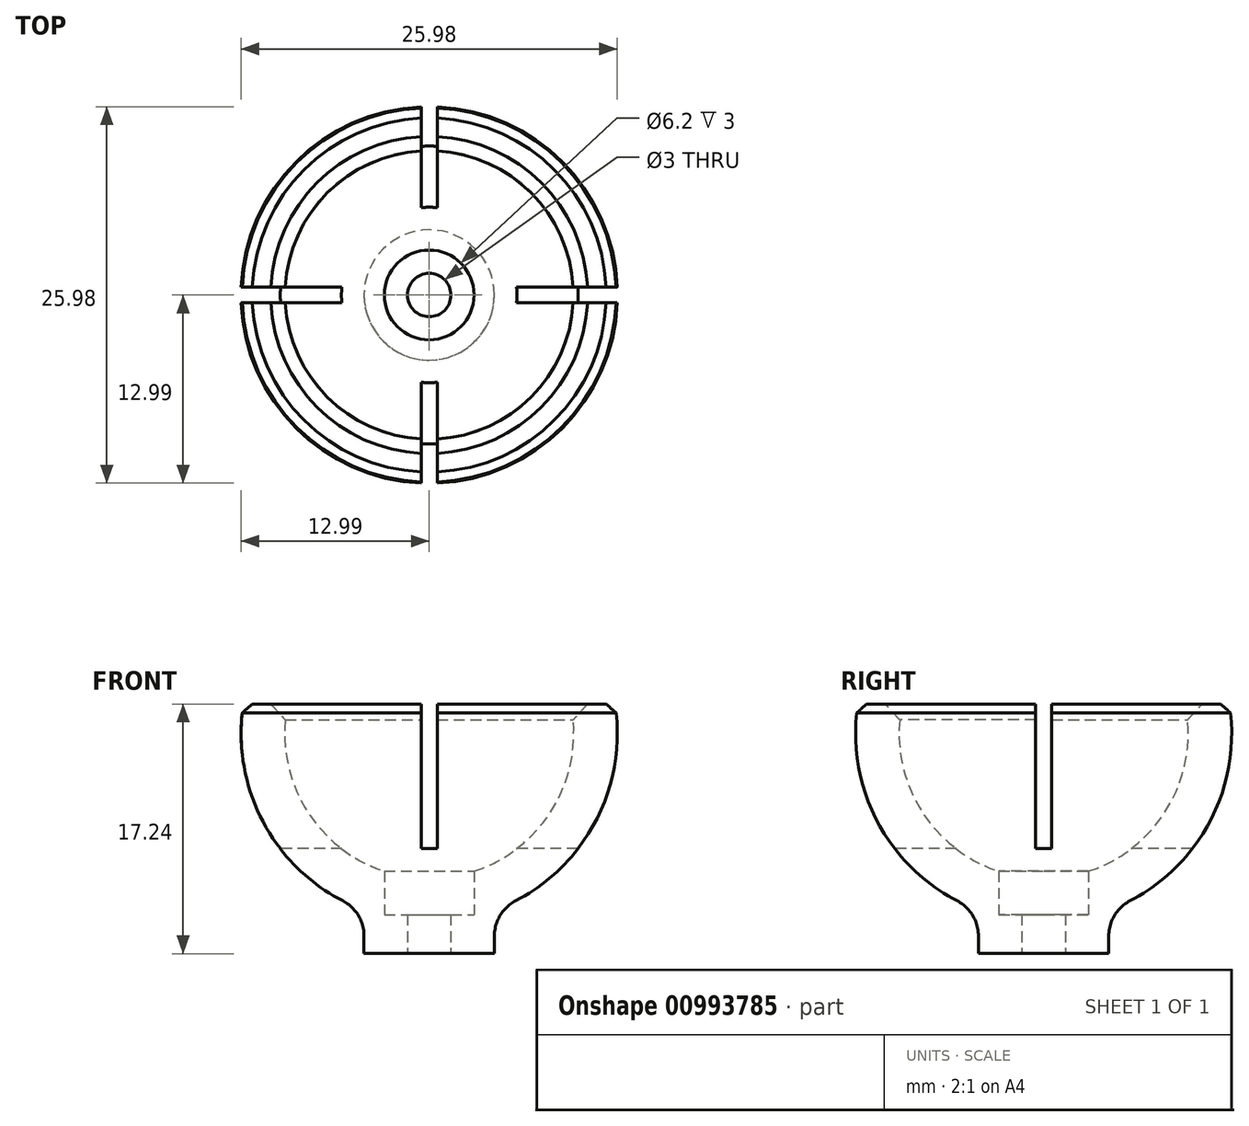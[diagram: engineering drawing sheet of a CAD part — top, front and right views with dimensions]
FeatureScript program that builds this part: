
annotation { "Feature Type Name" : "Feature", "Feature Type Description" : "" }
export const myFeature = defineFeature(function(context is Context, id is Id, definition is map)
    precondition{}
    {
        {
            var Q0;
            Q0=qCreatedBy(makeId("Front.planeOp"),FACE);
            var sketch = newSketch(context, id + "F0", { "sketchPlane" : qUnion([Q0])});
            skPoint(sketch, "E0.middle", {"position": v(0, 0) * mm});
            skArc(sketch, "E1", {"start": v(-9.79, 2.04) * mm, "mid": v(-8.65, -5.01) * mm, "end": v(-3.1, -9.5) * mm});
            skLineSegment(sketch, "E2", {"start": v(0, -15.2) * mm, "end": v(0, 34.9) * mm, "construction": true});
            skLineSegment(sketch, "E3", {"start": v(-4.5, -12.2) * mm, "end": v(-4.5, -15.2) * mm});
            skArc(sketch, "E4.0", {"start": v(-12.84, 2.04) * mm, "mid": v(-11.22, -6.57) * mm, "end": v(-4.5, -12.2) * mm});
            skPoint(sketch, "E5", {"position": v(-10, 0) * mm});
            skLineSegment(sketch, "E6", {"start": v(-4.5, -15.2) * mm, "end": v(-1.5, -15.2) * mm});
            skLineSegment(sketch, "E7", {"start": v(-3.1, -9.5) * mm, "end": v(-3.1, -12.5) * mm});
            skLineSegment(sketch, "E8", {"start": v(-3.1, -12.5) * mm, "end": v(-1.5, -12.5) * mm});
            skLineSegment(sketch, "E9", {"start": v(-1.5, -12.5) * mm, "end": v(-1.5, -15.2) * mm});
            skPoint(sketch, "E10.orphan", {"position": v(0, -10) * mm});
            skLineSegment(sketch, "E11", {"start": v(-9.79, 2.04) * mm, "end": v(-12.84, 2.04) * mm});
            skSolve(sketch);
        }
        {
            var Q0;
            Q0 = qSketchRegion(id + "F0", true);
            var Q1;
            Q1=sQuery(id+"F0.wireOp",EDGE,"E2");
            revolve(context, id + "F1", {"surfaceOperationType" : NewSurfaceOperationType.NEW, "entities" : qUnion([Q0]), "axis" : qUnion([Q1]), "revolveType" : RevolveType.FULL});
        }
        {
            var Q0;
            Q0=makeQuery(id+"F1.opRevolve","SWEPT_FACE",FACE,{"disambiguationData":[OSD([sQuery(id+"F0.wireOp",EDGE,"E11")])]});
            var sketch = newSketch(context, id + "F2", { "sketchPlane" : qUnion([Q0])});
            skLineSegment(sketch, "E12.bottom", {"start": v(13.5, 0.55) * mm, "end": v(-13.5, 0.55) * mm});
            skLineSegment(sketch, "E12.top", {"start": v(13.5, -0.55) * mm, "end": v(-13.5, -0.55) * mm});
            skLineSegment(sketch, "E12.left", {"start": v(13.5, 0.55) * mm, "end": v(13.5, -0.55) * mm});
            skLineSegment(sketch, "E12.right", {"start": v(-13.5, 0.55) * mm, "end": v(-13.5, -0.55) * mm});
            skPoint(sketch, "E12.middle", {"position": v(0, 0) * mm});
            skLineSegment(sketch, "E13.bottom", {"start": v(-0.55, 13.5) * mm, "end": v(0.55, 13.5) * mm});
            skLineSegment(sketch, "E13.top", {"start": v(-0.55, -13.5) * mm, "end": v(0.55, -13.5) * mm});
            skLineSegment(sketch, "E13.left", {"start": v(-0.55, 13.5) * mm, "end": v(-0.55, -13.5) * mm});
            skLineSegment(sketch, "E13.right", {"start": v(0.55, 13.5) * mm, "end": v(0.55, -13.5) * mm});
            skSolve(sketch);
        }
        {
            var Q0;
            Q0 = qSketchRegion(id + "F2", true);
            extrude(context, id + "F3", {"entities" : qUnion([Q0]), "operationType" : NewBodyOperationType.REMOVE, "oppositeDirection" : true, "depth" : 10 * mm, "offsetDistance" : 25 * mm});
        }
        {
            var Q0;
            {var subQ0=sQuery(id+"F0.wireOp",EDGE,"E4.0");var subQ1=sQuery(id+"F0.wireOp",EDGE,"E11");var subQ2=sQuery(id+"F2.wireOp",EDGE,"E13.right");var subQ3=sQuery(id+"F2.wireOp",EDGE,"E12.bottom");var subQ4=makeQuery(id+"F2.imprint","INTERSECT",VERTEX,{"derivedFrom":[subQ3,subQ2]});var subQ7=makeQuery(id+"F1.opRevolve","SWEPT_EDGE",EDGE,{"disambiguationData":[OSD([subQ0,subQ1])]});var subQ8=makeQuery(id+"F2.imprint","INTERSECT",VERTEX,{"disambiguationData":[OD(0.0)],"derivedFrom":[subQ7,subQ3]});Q0=makeQuery(id+"F3.boolean.opBoolean","SPLIT",EDGE,{"disambiguationData":[TD([makeQuery(id+"F3.opExtrude","SWEPT_FACE",FACE,{"disambiguationData":[OSD([subQ3]),TDD([makeQuery(id+"F2.imprint","IMPRINT",EDGE,{"disambiguationData":[TD([[makeQuery(id+"F2.imprint","INTERSECT",VERTEX,{"derivedFrom":[subQ3,sQuery(id+"F2.wireOp",EDGE,"E12.left")]}),-1.0]])],"derivedFrom":subQ3}),makeQuery(id+"F2.imprint","IMPRINT",EDGE,{"disambiguationData":[TD([[subQ8,-1.0]])],"derivedFrom":subQ3}),makeQuery(id+"F2.imprint","IMPRINT",EDGE,{"disambiguationData":[TD([[subQ4,1.0]])],"derivedFrom":subQ3})])]})])],"derivedFrom":subQ7});}
            var Q1;
            {var subQ0=sQuery(id+"F0.wireOp",EDGE,"E4.0");var subQ1=sQuery(id+"F0.wireOp",EDGE,"E11");var subQ2=sQuery(id+"F2.wireOp",EDGE,"E13.right");var subQ3=sQuery(id+"F2.wireOp",EDGE,"E12.top");var subQ4=makeQuery(id+"F2.imprint","INTERSECT",VERTEX,{"derivedFrom":[subQ3,subQ2]});var subQ7=makeQuery(id+"F1.opRevolve","SWEPT_EDGE",EDGE,{"disambiguationData":[OSD([subQ0,subQ1])]});var subQ8=makeQuery(id+"F2.imprint","INTERSECT",VERTEX,{"disambiguationData":[OD(0.0)],"derivedFrom":[subQ7,subQ3]});Q1=makeQuery(id+"F3.boolean.opBoolean","SPLIT",EDGE,{"disambiguationData":[TD([makeQuery(id+"F3.opExtrude","SWEPT_FACE",FACE,{"disambiguationData":[OSD([subQ3]),TDD([makeQuery(id+"F2.imprint","IMPRINT",EDGE,{"disambiguationData":[TD([[makeQuery(id+"F2.imprint","INTERSECT",VERTEX,{"derivedFrom":[subQ3,sQuery(id+"F2.wireOp",EDGE,"E12.left")]}),-1.0]])],"derivedFrom":subQ3}),makeQuery(id+"F2.imprint","IMPRINT",EDGE,{"disambiguationData":[TD([[subQ8,-1.0]])],"derivedFrom":subQ3}),makeQuery(id+"F2.imprint","IMPRINT",EDGE,{"disambiguationData":[TD([[subQ4,1.0]])],"derivedFrom":subQ3})])]})])],"derivedFrom":subQ7});}
            var Q2;
            {var subQ0=sQuery(id+"F0.wireOp",EDGE,"E4.0");var subQ1=sQuery(id+"F0.wireOp",EDGE,"E11");var subQ2=sQuery(id+"F2.wireOp",EDGE,"E12.bottom");var subQ3=makeQuery(id+"F1.opRevolve","SWEPT_EDGE",EDGE,{"disambiguationData":[OSD([subQ0,subQ1])]});var subQ4=makeQuery(id+"F2.imprint","INTERSECT",VERTEX,{"disambiguationData":[OD(1.0)],"derivedFrom":[subQ3,subQ2]});var subQ7=sQuery(id+"F2.wireOp",EDGE,"E13.left");var subQ8=makeQuery(id+"F2.imprint","INTERSECT",VERTEX,{"derivedFrom":[subQ2,subQ7]});Q2=makeQuery(id+"F3.boolean.opBoolean","SPLIT",EDGE,{"disambiguationData":[TD([makeQuery(id+"F3.opExtrude","SWEPT_FACE",FACE,{"disambiguationData":[OSD([subQ2]),TDD([makeQuery(id+"F2.imprint","IMPRINT",EDGE,{"disambiguationData":[TD([[subQ8,-1.0]])],"derivedFrom":subQ2}),makeQuery(id+"F2.imprint","IMPRINT",EDGE,{"disambiguationData":[TD([[subQ4,1.0]])],"derivedFrom":subQ2}),makeQuery(id+"F2.imprint","IMPRINT",EDGE,{"disambiguationData":[TD([[makeQuery(id+"F2.imprint","INTERSECT",VERTEX,{"derivedFrom":[subQ2,sQuery(id+"F2.wireOp",EDGE,"E12.right")]}),1.0]])],"derivedFrom":subQ2})])]})])],"derivedFrom":subQ3});}
            var Q3;
            {var subQ0=sQuery(id+"F0.wireOp",EDGE,"E4.0");var subQ1=sQuery(id+"F0.wireOp",EDGE,"E11");var subQ2=sQuery(id+"F2.wireOp",EDGE,"E12.top");var subQ3=makeQuery(id+"F1.opRevolve","SWEPT_EDGE",EDGE,{"disambiguationData":[OSD([subQ0,subQ1])]});var subQ4=makeQuery(id+"F2.imprint","INTERSECT",VERTEX,{"disambiguationData":[OD(1.0)],"derivedFrom":[subQ3,subQ2]});var subQ7=sQuery(id+"F2.wireOp",EDGE,"E13.left");var subQ8=makeQuery(id+"F2.imprint","INTERSECT",VERTEX,{"derivedFrom":[subQ2,subQ7]});Q3=makeQuery(id+"F3.boolean.opBoolean","SPLIT",EDGE,{"disambiguationData":[TD([makeQuery(id+"F3.opExtrude","SWEPT_FACE",FACE,{"disambiguationData":[OSD([subQ2]),TDD([makeQuery(id+"F2.imprint","IMPRINT",EDGE,{"disambiguationData":[TD([[subQ8,-1.0]])],"derivedFrom":subQ2}),makeQuery(id+"F2.imprint","IMPRINT",EDGE,{"disambiguationData":[TD([[subQ4,1.0]])],"derivedFrom":subQ2}),makeQuery(id+"F2.imprint","IMPRINT",EDGE,{"disambiguationData":[TD([[makeQuery(id+"F2.imprint","INTERSECT",VERTEX,{"derivedFrom":[subQ2,sQuery(id+"F2.wireOp",EDGE,"E12.right")]}),1.0]])],"derivedFrom":subQ2})])]})])],"derivedFrom":subQ3});}
            chamfer(context, id + "F4", {"entities" : qUnion([Q0, Q1, Q2, Q3]), "width" : 0.7 * mm, "tangentPropagation" : true});
        }
        {
            var Q0;
            {var subQ0=sQuery(id+"F0.wireOp",EDGE,"E1");var subQ1=sQuery(id+"F0.wireOp",EDGE,"E11");var subQ2=sQuery(id+"F2.wireOp",EDGE,"E13.right");var subQ3=sQuery(id+"F2.wireOp",EDGE,"E12.top");var subQ4=makeQuery(id+"F2.imprint","INTERSECT",VERTEX,{"derivedFrom":[subQ3,subQ2]});var subQ5=makeQuery(id+"F1.opRevolve","SWEPT_EDGE",EDGE,{"disambiguationData":[OSD([subQ0,subQ1])]});var subQ7=makeQuery(id+"F1.opRevolve","SWEPT_EDGE",EDGE,{"disambiguationData":[OSD([sQuery(id+"F0.wireOp",EDGE,"E4.0"),subQ1])]});var subQ8=makeQuery(id+"F2.imprint","INTERSECT",VERTEX,{"disambiguationData":[OD(0.0)],"derivedFrom":[subQ7,subQ3]});Q0=makeQuery(id+"F3.boolean.opBoolean","SPLIT",EDGE,{"disambiguationData":[TD([makeQuery(id+"F3.opExtrude","SWEPT_FACE",FACE,{"disambiguationData":[OSD([subQ3]),TDD([makeQuery(id+"F2.imprint","IMPRINT",EDGE,{"disambiguationData":[TD([[makeQuery(id+"F2.imprint","INTERSECT",VERTEX,{"derivedFrom":[subQ3,sQuery(id+"F2.wireOp",EDGE,"E12.left")]}),-1.0]])],"derivedFrom":subQ3}),makeQuery(id+"F2.imprint","IMPRINT",EDGE,{"disambiguationData":[TD([[subQ8,-1.0]])],"derivedFrom":subQ3}),makeQuery(id+"F2.imprint","IMPRINT",EDGE,{"disambiguationData":[TD([[subQ4,1.0]])],"derivedFrom":subQ3})])]})])],"derivedFrom":subQ5});}
            var Q1;
            {var subQ0=sQuery(id+"F0.wireOp",EDGE,"E1");var subQ1=sQuery(id+"F0.wireOp",EDGE,"E11");var subQ2=sQuery(id+"F2.wireOp",EDGE,"E12.top");var subQ3=makeQuery(id+"F1.opRevolve","SWEPT_EDGE",EDGE,{"disambiguationData":[OSD([sQuery(id+"F0.wireOp",EDGE,"E4.0"),subQ1])]});var subQ4=makeQuery(id+"F2.imprint","INTERSECT",VERTEX,{"disambiguationData":[OD(1.0)],"derivedFrom":[subQ3,subQ2]});var subQ5=makeQuery(id+"F1.opRevolve","SWEPT_EDGE",EDGE,{"disambiguationData":[OSD([subQ0,subQ1])]});var subQ7=sQuery(id+"F2.wireOp",EDGE,"E13.left");var subQ8=makeQuery(id+"F2.imprint","INTERSECT",VERTEX,{"derivedFrom":[subQ2,subQ7]});Q1=makeQuery(id+"F3.boolean.opBoolean","SPLIT",EDGE,{"disambiguationData":[TD([makeQuery(id+"F3.opExtrude","SWEPT_FACE",FACE,{"disambiguationData":[OSD([subQ2]),TDD([makeQuery(id+"F2.imprint","IMPRINT",EDGE,{"disambiguationData":[TD([[subQ8,-1.0]])],"derivedFrom":subQ2}),makeQuery(id+"F2.imprint","IMPRINT",EDGE,{"disambiguationData":[TD([[subQ4,1.0]])],"derivedFrom":subQ2}),makeQuery(id+"F2.imprint","IMPRINT",EDGE,{"disambiguationData":[TD([[makeQuery(id+"F2.imprint","INTERSECT",VERTEX,{"derivedFrom":[subQ2,sQuery(id+"F2.wireOp",EDGE,"E12.right")]}),1.0]])],"derivedFrom":subQ2})])]})])],"derivedFrom":subQ5});}
            var Q2;
            {var subQ0=sQuery(id+"F0.wireOp",EDGE,"E1");var subQ1=sQuery(id+"F0.wireOp",EDGE,"E11");var subQ2=sQuery(id+"F2.wireOp",EDGE,"E12.bottom");var subQ3=makeQuery(id+"F1.opRevolve","SWEPT_EDGE",EDGE,{"disambiguationData":[OSD([sQuery(id+"F0.wireOp",EDGE,"E4.0"),subQ1])]});var subQ4=makeQuery(id+"F2.imprint","INTERSECT",VERTEX,{"disambiguationData":[OD(1.0)],"derivedFrom":[subQ3,subQ2]});var subQ5=makeQuery(id+"F1.opRevolve","SWEPT_EDGE",EDGE,{"disambiguationData":[OSD([subQ0,subQ1])]});var subQ7=sQuery(id+"F2.wireOp",EDGE,"E13.left");var subQ8=makeQuery(id+"F2.imprint","INTERSECT",VERTEX,{"derivedFrom":[subQ2,subQ7]});Q2=makeQuery(id+"F3.boolean.opBoolean","SPLIT",EDGE,{"disambiguationData":[TD([makeQuery(id+"F3.opExtrude","SWEPT_FACE",FACE,{"disambiguationData":[OSD([subQ2]),TDD([makeQuery(id+"F2.imprint","IMPRINT",EDGE,{"disambiguationData":[TD([[subQ8,-1.0]])],"derivedFrom":subQ2}),makeQuery(id+"F2.imprint","IMPRINT",EDGE,{"disambiguationData":[TD([[subQ4,1.0]])],"derivedFrom":subQ2}),makeQuery(id+"F2.imprint","IMPRINT",EDGE,{"disambiguationData":[TD([[makeQuery(id+"F2.imprint","INTERSECT",VERTEX,{"derivedFrom":[subQ2,sQuery(id+"F2.wireOp",EDGE,"E12.right")]}),1.0]])],"derivedFrom":subQ2})])]})])],"derivedFrom":subQ5});}
            var Q3;
            {var subQ0=sQuery(id+"F0.wireOp",EDGE,"E1");var subQ1=sQuery(id+"F2.wireOp",EDGE,"E13.right");var subQ2=sQuery(id+"F2.wireOp",EDGE,"E12.bottom");var subQ3=makeQuery(id+"F2.imprint","INTERSECT",VERTEX,{"derivedFrom":[subQ2,subQ1]});var subQ4=sQuery(id+"F0.wireOp",EDGE,"E11");var subQ5=makeQuery(id+"F1.opRevolve","SWEPT_EDGE",EDGE,{"disambiguationData":[OSD([subQ0,subQ4])]});var subQ7=makeQuery(id+"F1.opRevolve","SWEPT_EDGE",EDGE,{"disambiguationData":[OSD([sQuery(id+"F0.wireOp",EDGE,"E4.0"),subQ4])]});var subQ10=makeQuery(id+"F2.imprint","INTERSECT",VERTEX,{"disambiguationData":[OD(0.0)],"derivedFrom":[subQ7,subQ2]});Q3=makeQuery(id+"F3.boolean.opBoolean","SPLIT",EDGE,{"disambiguationData":[TD([makeQuery(id+"F3.opExtrude","SWEPT_FACE",FACE,{"disambiguationData":[OSD([subQ2]),TDD([makeQuery(id+"F2.imprint","IMPRINT",EDGE,{"disambiguationData":[TD([[makeQuery(id+"F2.imprint","INTERSECT",VERTEX,{"derivedFrom":[subQ2,sQuery(id+"F2.wireOp",EDGE,"E12.left")]}),-1.0]])],"derivedFrom":subQ2}),makeQuery(id+"F2.imprint","IMPRINT",EDGE,{"disambiguationData":[TD([[subQ10,-1.0]])],"derivedFrom":subQ2}),makeQuery(id+"F2.imprint","IMPRINT",EDGE,{"disambiguationData":[TD([[subQ3,1.0]])],"derivedFrom":subQ2})])]})])],"derivedFrom":subQ5});}
            chamfer(context, id + "F5", {"entities" : qUnion([Q0, Q1, Q2, Q3]), "width" : 1 * mm, "tangentPropagation" : true});
        }
        {
            var Q0;
            Q0=makeQuery(id+"F1.opRevolve","SWEPT_EDGE",EDGE,{"disambiguationData":[OSD([sQuery(id+"F0.wireOp",EDGE,"E3"),sQuery(id+"F0.wireOp",EDGE,"E4.0")])]});
            fillet(context, id + "F6", {"entities" : qUnion([Q0]), "radius" : 2.74 * mm, "tangentPropagation" : true, "allowEdgeOverflow" : false});
        }
    });
